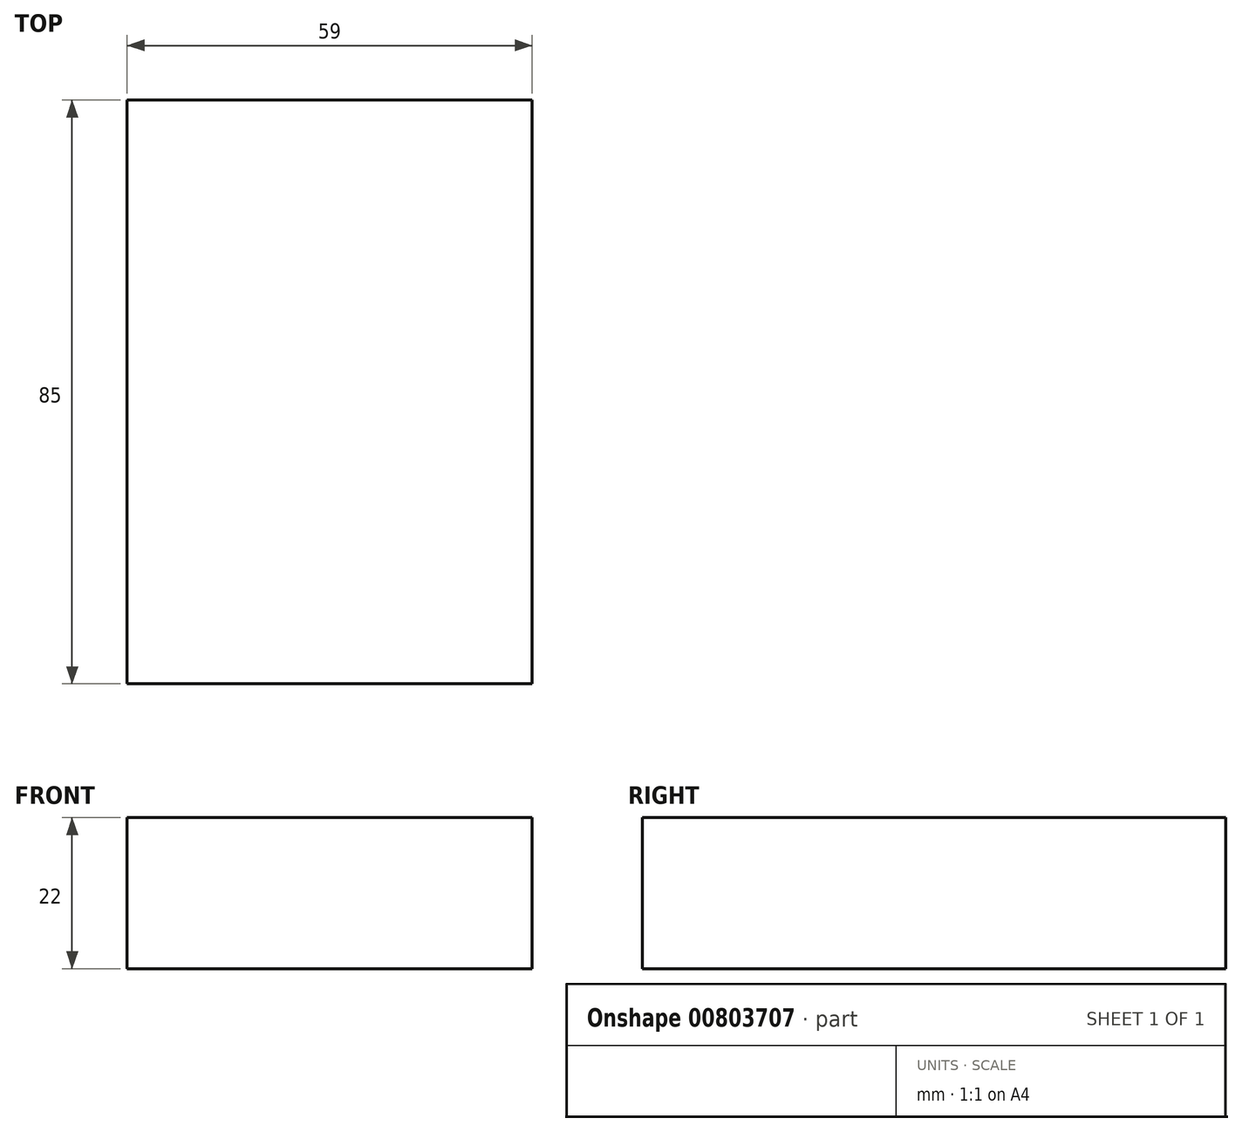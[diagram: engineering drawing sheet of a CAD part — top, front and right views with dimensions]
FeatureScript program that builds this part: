
annotation { "Feature Type Name" : "Feature", "Feature Type Description" : "" }
export const myFeature = defineFeature(function(context is Context, id is Id, definition is map)
    precondition{}
    {
        {
            var Q0;
            Q0=qCreatedBy(makeId("Top.planeOp"),FACE);
            var sketch = newSketch(context, id + "F0", { "sketchPlane" : qUnion([Q0])});
            skLineSegment(sketch, "E0.bottom", {"start": v(-28.58, 43.95) * mm, "end": v(30.42, 43.95) * mm});
            skLineSegment(sketch, "E0.top", {"start": v(-28.58, -41.05) * mm, "end": v(30.42, -41.05) * mm});
            skLineSegment(sketch, "E0.left", {"start": v(-28.58, 43.95) * mm, "end": v(-28.58, -41.05) * mm});
            skLineSegment(sketch, "E0.right", {"start": v(30.42, 43.95) * mm, "end": v(30.42, -41.05) * mm});
            skSolve(sketch);
        }
        {
            var Q0;
            Q0 = qSketchRegion(id + "F0", true);
            extrude(context, id + "F1", {"entities" : qUnion([Q0]), "depth" : 22 * mm, "offsetDistance" : 25 * mm});
        }
    });
